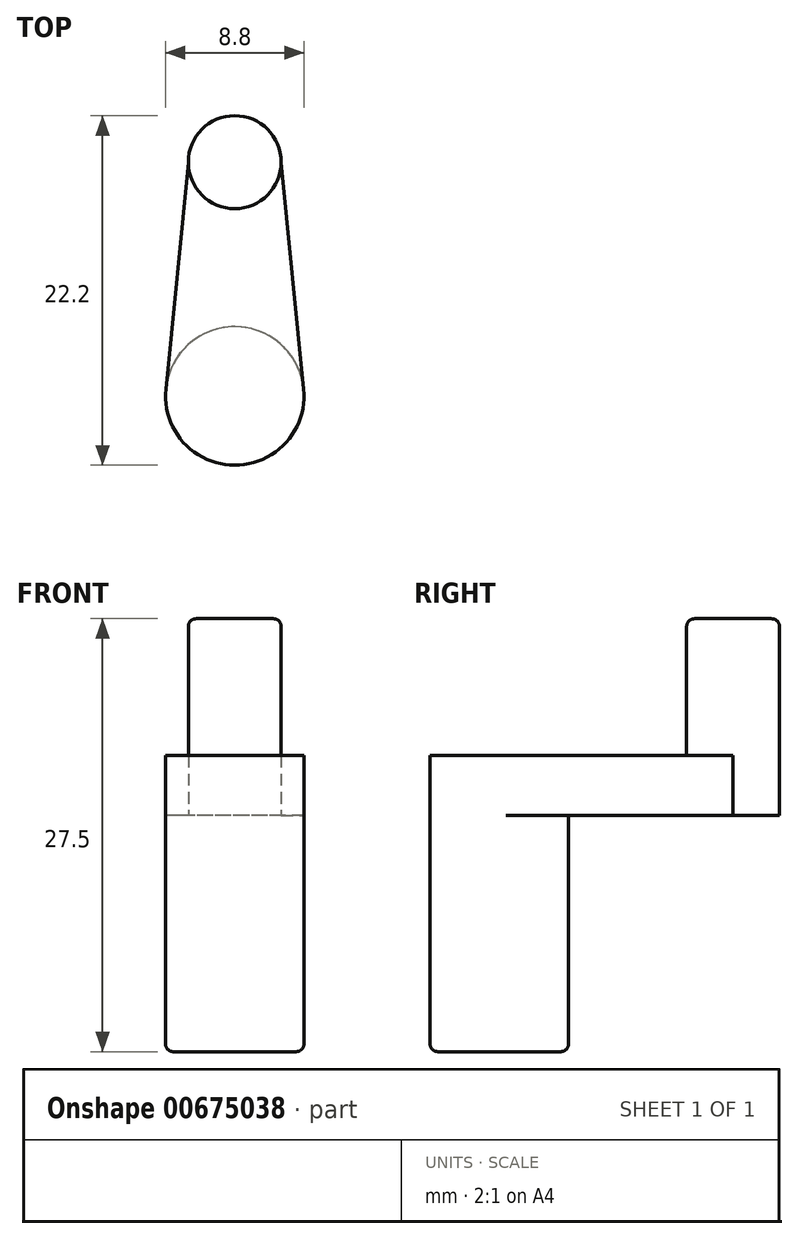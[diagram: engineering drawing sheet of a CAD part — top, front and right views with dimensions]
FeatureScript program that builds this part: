
annotation { "Feature Type Name" : "Feature", "Feature Type Description" : "" }
export const myFeature = defineFeature(function(context is Context, id is Id, definition is map)
    precondition{}
    {
        {
            var Q0;
            Q0=qCreatedBy(makeId("Top.planeOp"),FACE);
            var sketch = newSketch(context, id + "F0", { "sketchPlane" : qUnion([Q0])});
            skCircle(sketch, "E0", {"center": v(0, 0) * mm, "radius": 2.95 * mm});
            skCircle(sketch, "E1", {"center": v(0, -14.85) * mm, "radius": 4.4 * mm});
            skLineSegment(sketch, "E2", {"start": v(-2.95, 0) * mm, "end": v(-4.38, -14.42) * mm});
            skLineSegment(sketch, "E3.MirrorCS", {"start": v(2.95, 0) * mm, "end": v(4.38, -14.42) * mm});
            skSolve(sketch);
        }
        {
            var Q0;
            {var subQ0=sQuery(id+"F0.wireOp",EDGE,"E2");Q0=makeQuery(id+"F0.imprint","IMPRINT",FACE,{"disambiguationData":[TD([[makeQuery(id+"F0.imprint","IMPRINT",EDGE,{"derivedFrom":subQ0}),1.0]])]});}
            var Q1;
            {var subQ0=sQuery(id+"F0.wireOp",EDGE,"E1");var subQ1=makeQuery(id+"F0.imprint","INTERSECT",VERTEX,{"derivedFrom":[subQ0,sQuery(id+"F0.wireOp",EDGE,"E2")]});Q1=makeQuery(id+"F0.imprint","IMPRINT",FACE,{"disambiguationData":[TD([[makeQuery(id+"F0.imprint","IMPRINT",EDGE,{"disambiguationData":[TD([[subQ1,1.0]])],"derivedFrom":subQ0}),1.0]])]});}
            var Q2;
            {var subQ0=sQuery(id+"F0.wireOp",EDGE,"E0");var subQ1=makeQuery(id+"F0.imprint","INTERSECT",VERTEX,{"derivedFrom":[subQ0,sQuery(id+"F0.wireOp",EDGE,"E2")]});Q2=makeQuery(id+"F0.imprint","IMPRINT",FACE,{"disambiguationData":[TD([[makeQuery(id+"F0.imprint","IMPRINT",EDGE,{"disambiguationData":[TD([[subQ1,1.0]])],"derivedFrom":subQ0}),1.0]])]});}
            extrude(context, id + "F1", {"entities" : qUnion([Q0, Q1, Q2]), "depth" : 3.8 * mm, "offsetDistance" : 25 * mm});
        }
        {
            var Q0;
            {var subQ0=sQuery(id+"F0.wireOp",EDGE,"E0");var subQ1=makeQuery(id+"F0.imprint","INTERSECT",VERTEX,{"derivedFrom":[subQ0,sQuery(id+"F0.wireOp",EDGE,"E2")]});Q0=makeQuery(id+"F0.imprint","IMPRINT",FACE,{"disambiguationData":[TD([[makeQuery(id+"F0.imprint","IMPRINT",EDGE,{"disambiguationData":[TD([[subQ1,1.0]])],"derivedFrom":subQ0}),1.0]])]});}
            extrude(context, id + "F2", {"entities" : qUnion([Q0]), "operationType" : NewBodyOperationType.ADD, "depth" : 12.5 * mm, "offsetDistance" : 25 * mm});
        }
        {
            var Q0;
            {var subQ0=sQuery(id+"F0.wireOp",EDGE,"E1");var subQ1=makeQuery(id+"F0.imprint","INTERSECT",VERTEX,{"derivedFrom":[subQ0,sQuery(id+"F0.wireOp",EDGE,"E2")]});Q0=makeQuery(id+"F0.imprint","IMPRINT",FACE,{"disambiguationData":[TD([[makeQuery(id+"F0.imprint","IMPRINT",EDGE,{"disambiguationData":[TD([[subQ1,1.0]])],"derivedFrom":subQ0}),1.0]])]});}
            extrude(context, id + "F3", {"entities" : qUnion([Q0]), "operationType" : NewBodyOperationType.ADD, "oppositeDirection" : true, "depth" : 15 * mm, "offsetDistance" : 25 * mm});
        }
        {
            var Q0;
            Q0=makeQuery(id+"F2.opExtrude","CAP_EDGE",EDGE,{"disambiguationData":[OSD([sQuery(id+"F0.wireOp",EDGE,"E0")])],"isStart":false});
            var Q1;
            Q1=makeQuery(id+"F3.opExtrude","CAP_EDGE",EDGE,{"disambiguationData":[OSD([sQuery(id+"F0.wireOp",EDGE,"E1")])],"isStart":false});
            fillet(context, id + "F4", {"entities" : qUnion([Q0, Q1]), "radius" : 0.5 * mm, "tangentPropagation" : true, "allowEdgeOverflow" : false});
        }
    });
